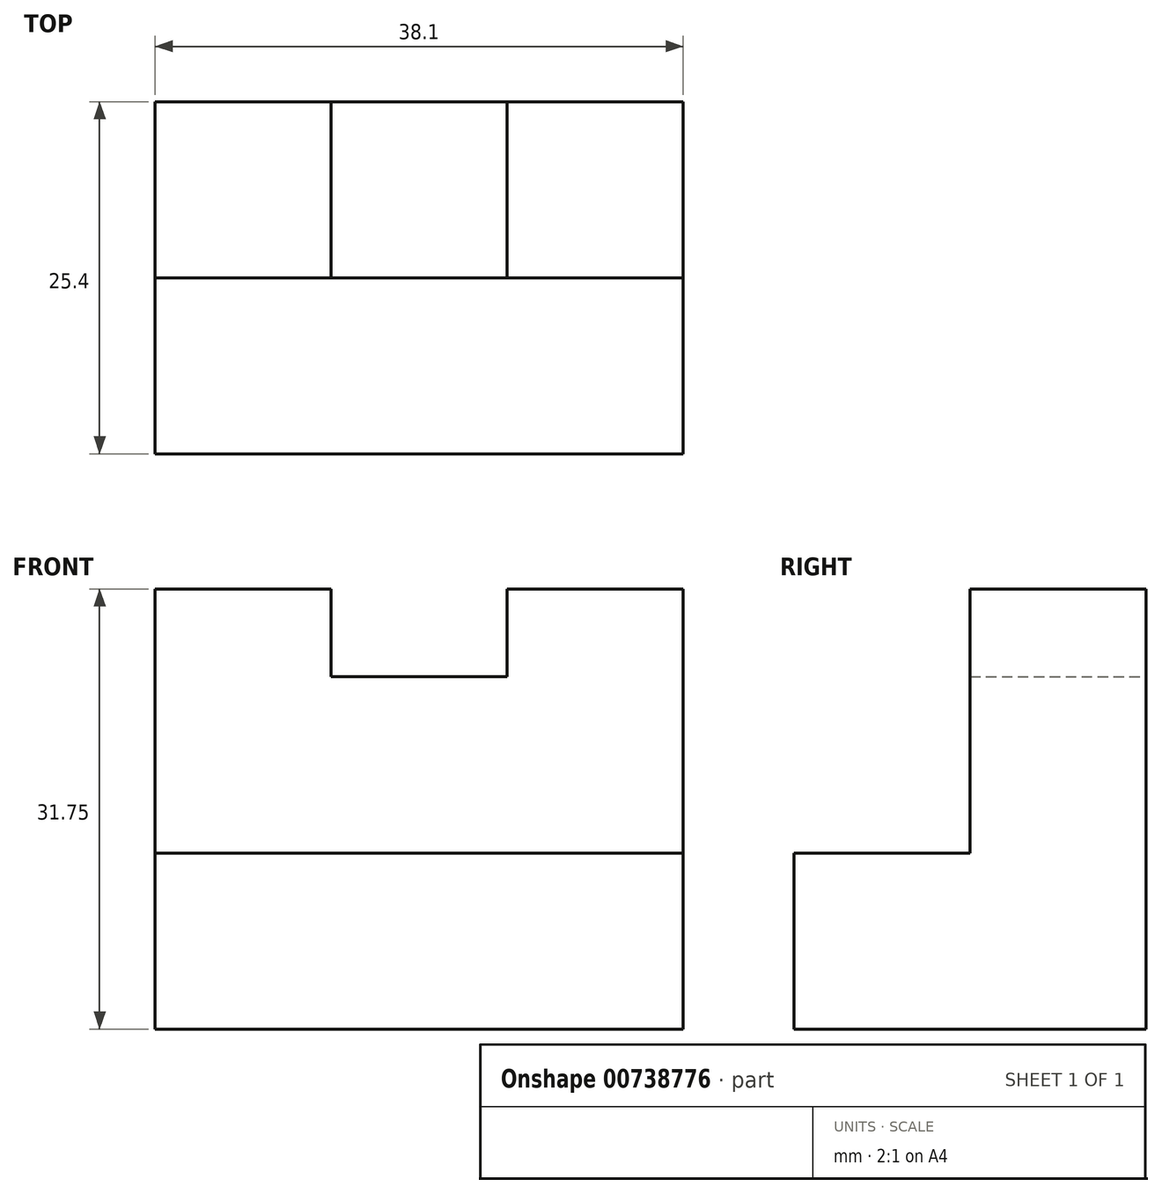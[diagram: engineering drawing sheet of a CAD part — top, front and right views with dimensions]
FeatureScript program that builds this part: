
annotation { "Feature Type Name" : "Feature", "Feature Type Description" : "" }
export const myFeature = defineFeature(function(context is Context, id is Id, definition is map)
    precondition{}
    {
        {
            var Q0;
            Q0=qCreatedBy(makeId("Right.planeOp"),FACE);
            var sketch = newSketch(context, id + "F0", { "sketchPlane" : qUnion([Q0])});
            skLineSegment(sketch, "E0", {"start": v(0, 31.75) * mm, "end": v(0, 0) * mm});
            skLineSegment(sketch, "E1", {"start": v(0, 0) * mm, "end": v(-25.4, 0) * mm});
            skLineSegment(sketch, "E2", {"start": v(-25.4, 0) * mm, "end": v(-25.4, 12.7) * mm});
            skLineSegment(sketch, "E3", {"start": v(-25.4, 12.7) * mm, "end": v(-12.7, 12.7) * mm});
            skLineSegment(sketch, "E4", {"start": v(-12.7, 12.7) * mm, "end": v(-12.7, 31.75) * mm});
            skLineSegment(sketch, "E5", {"start": v(-12.7, 31.75) * mm, "end": v(0, 31.75) * mm});
            skSolve(sketch);
        }
        {
            var Q0;
            Q0 = qSketchRegion(id + "F0", true);
            extrude(context, id + "F1", {"entities" : qUnion([Q0]), "depth" : 38.1 * mm, "offsetDistance" : 25.4 * mm});
        }
        {
            var Q0;
            Q0=qCreatedBy(makeId("Front.planeOp"),FACE);
            var sketch = newSketch(context, id + "F2", { "sketchPlane" : qUnion([Q0])});
            skLineSegment(sketch, "E6", {"start": v(12.7, 31.76) * mm, "end": v(12.7, 25.41) * mm});
            skLineSegment(sketch, "E7", {"start": v(12.7, 25.41) * mm, "end": v(25.4, 25.41) * mm});
            skLineSegment(sketch, "E8", {"start": v(25.4, 25.41) * mm, "end": v(25.4, 31.76) * mm});
            skLineSegment(sketch, "E9", {"start": v(25.4, 31.76) * mm, "end": v(12.7, 31.76) * mm});
            skSolve(sketch);
        }
        {
            var Q0;
            Q0=makeQuery(id+"F2.imprint","IMPRINT",FACE,{"disambiguationData":[TD([[makeQuery(id+"F2.imprint","IMPRINT",EDGE,{"derivedFrom":sQuery(id+"F2.wireOp",EDGE,"E6")}),1.0]])]});
            extrude(context, id + "F3", {"entities" : qUnion([Q0]), "operationType" : NewBodyOperationType.REMOVE, "depth" : 12.7 * mm, "offsetDistance" : 25.4 * mm});
        }
    });
